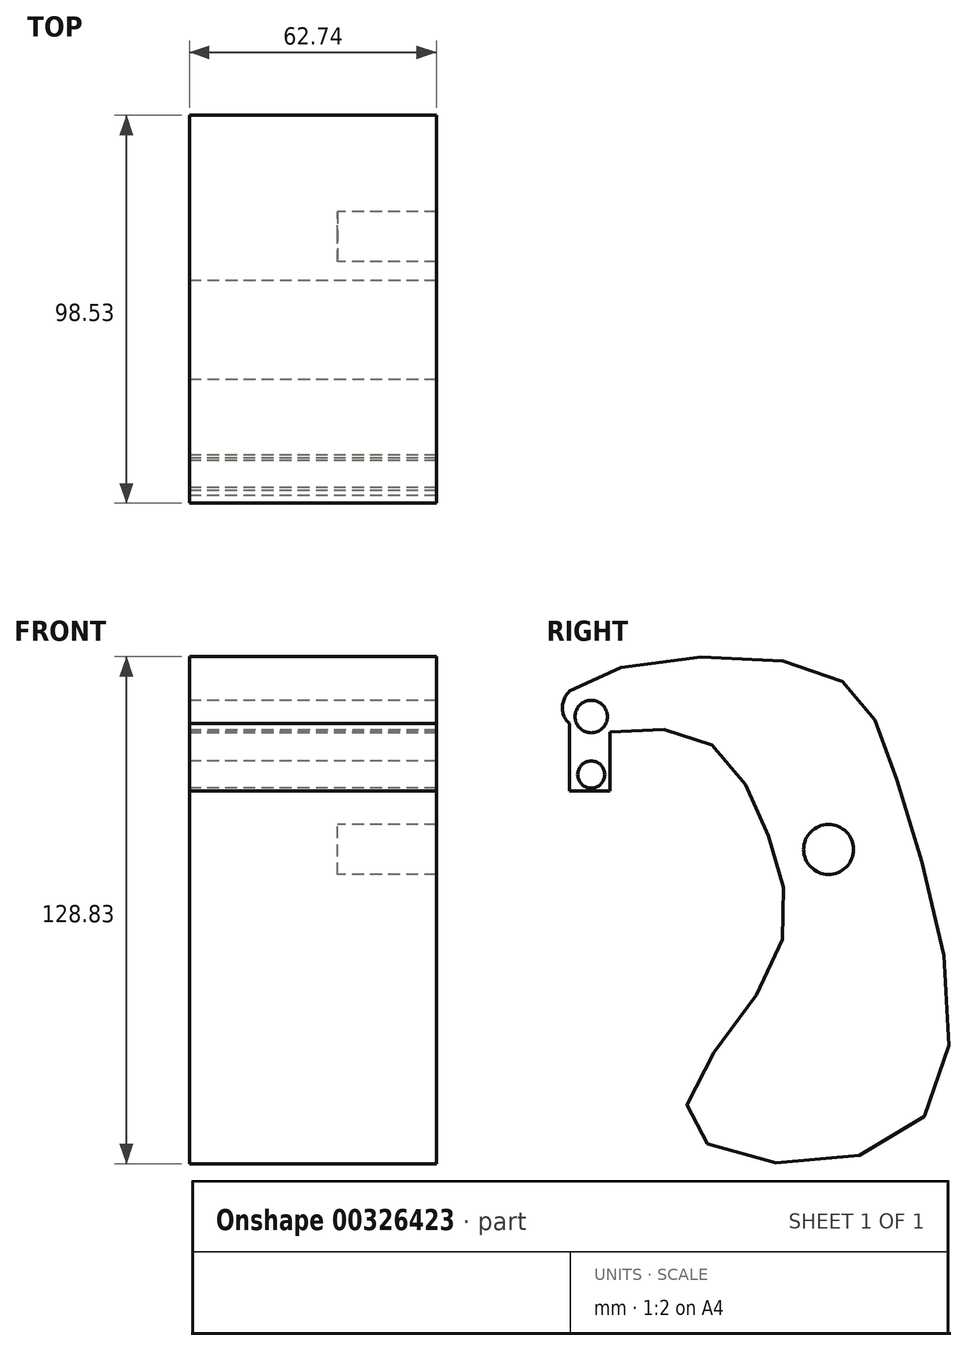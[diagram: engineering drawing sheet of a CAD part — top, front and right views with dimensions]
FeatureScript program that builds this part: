
annotation { "Feature Type Name" : "Feature", "Feature Type Description" : "" }
export const myFeature = defineFeature(function(context is Context, id is Id, definition is map)
    precondition{}
    {
        {
            var Q0;
            Q0=qCreatedBy(makeId("Right.planeOp"),FACE);
            var sketch = newSketch(context, id + "F0", { "sketchPlane" : qUnion([Q0])});
            skFitSpline(sketch, "E0", {"points": [v(-6.85, -70.43) * mm, v(-64.08, -70.43) * mm, v(-43.52, -31.02) * mm, v(-43.86, 2.9) * mm, v(-63.73, 29.3) * mm, v(-93.2, 31) * mm, v(-94.57, 40.26) * mm, v(-32.55, 46.09) * mm, v(-10.62, 14.9) * mm, v(-6.85, -70.43) * mm]});
            skLineSegment(sketch, "E1.bottom", {"start": v(-94.57, 40.26) * mm, "end": v(-84.3, 40.26) * mm});
            skLineSegment(sketch, "E1.top", {"start": v(-94.57, 14.9) * mm, "end": v(-84.3, 14.9) * mm});
            skLineSegment(sketch, "E1.left", {"start": v(-94.57, 40.26) * mm, "end": v(-94.57, 14.9) * mm});
            skLineSegment(sketch, "E1.right", {"start": v(-84.3, 40.26) * mm, "end": v(-84.3, 14.9) * mm});
            skCircle(sketch, "E2", {"center": v(-89.1, 19.01) * mm, "radius": 3.44 * mm});
            skCircle(sketch, "E3", {"center": v(-89.1, 33.75) * mm, "radius": 4.13 * mm});
            skSolve(sketch);
        }
        {
            var Q0;
            Q0 = qSketchRegion(id + "F0", true);
            extrude(context, id + "F1", {"entities" : qUnion([Q0]), "depth" : 37.34 * mm});
        }
        {
            var Q0;
            Q0=makeQuery(id+"F1.opExtrude","CAP_FACE",FACE,{"disambiguationData":[OSD([sQuery(id+"F0.wireOp",EDGE,"E0"),sQuery(id+"F0.wireOp",EDGE,"E1.top"),sQuery(id+"F0.wireOp",EDGE,"E1.left"),sQuery(id+"F0.wireOp",EDGE,"E1.right"),sQuery(id+"F0.wireOp",EDGE,"E2"),sQuery(id+"F0.wireOp",EDGE,"E3")])],"isStart":false});
            var sketch = newSketch(context, id + "F2", { "sketchPlane" : qUnion([Q0])});
            skCircle(sketch, "E4", {"center": v(-28.79, 0) * mm, "radius": 6.34 * mm});
            skSolve(sketch);
        }
        {
            var Q0;
            Q0 = qSketchRegion(id + "F2", true);
            extrude(context, id + "F3", {"entities" : qUnion([Q0]), "operationType" : NewBodyOperationType.ADD, "depth" : 0.25 * mm});
        }
        {
            var Q0;
            Q0=makeQuery(id+"F1.opExtrude","CAP_FACE",FACE,{"disambiguationData":[OSD([sQuery(id+"F0.wireOp",EDGE,"E0"),sQuery(id+"F0.wireOp",EDGE,"E1.top"),sQuery(id+"F0.wireOp",EDGE,"E1.left"),sQuery(id+"F0.wireOp",EDGE,"E1.right"),sQuery(id+"F0.wireOp",EDGE,"E2"),sQuery(id+"F0.wireOp",EDGE,"E3")])],"isStart":false});
            var sketch = newSketch(context, id + "F4", { "sketchPlane" : qUnion([Q0])});
            skSolve(sketch);
        }
        {
            var Q0;
            Q0=makeQuery(id+"F4.imprint","IMPRINT",FACE,{"disambiguationData":[TD([[makeQuery(id+"F4.imprint","IMPRINT",EDGE,{"derivedFrom":makeQuery(id+"F1.opExtrude","CAP_EDGE",EDGE,{"disambiguationData":[OSD([sQuery(id+"F0.wireOp",EDGE,"E0")])],"isStart":false})}),-1.0]])]});
            extrude(context, id + "F5", {"entities" : qUnion([Q0]), "operationType" : NewBodyOperationType.ADD, "depth" : 25.4 * mm});
        }
    });
